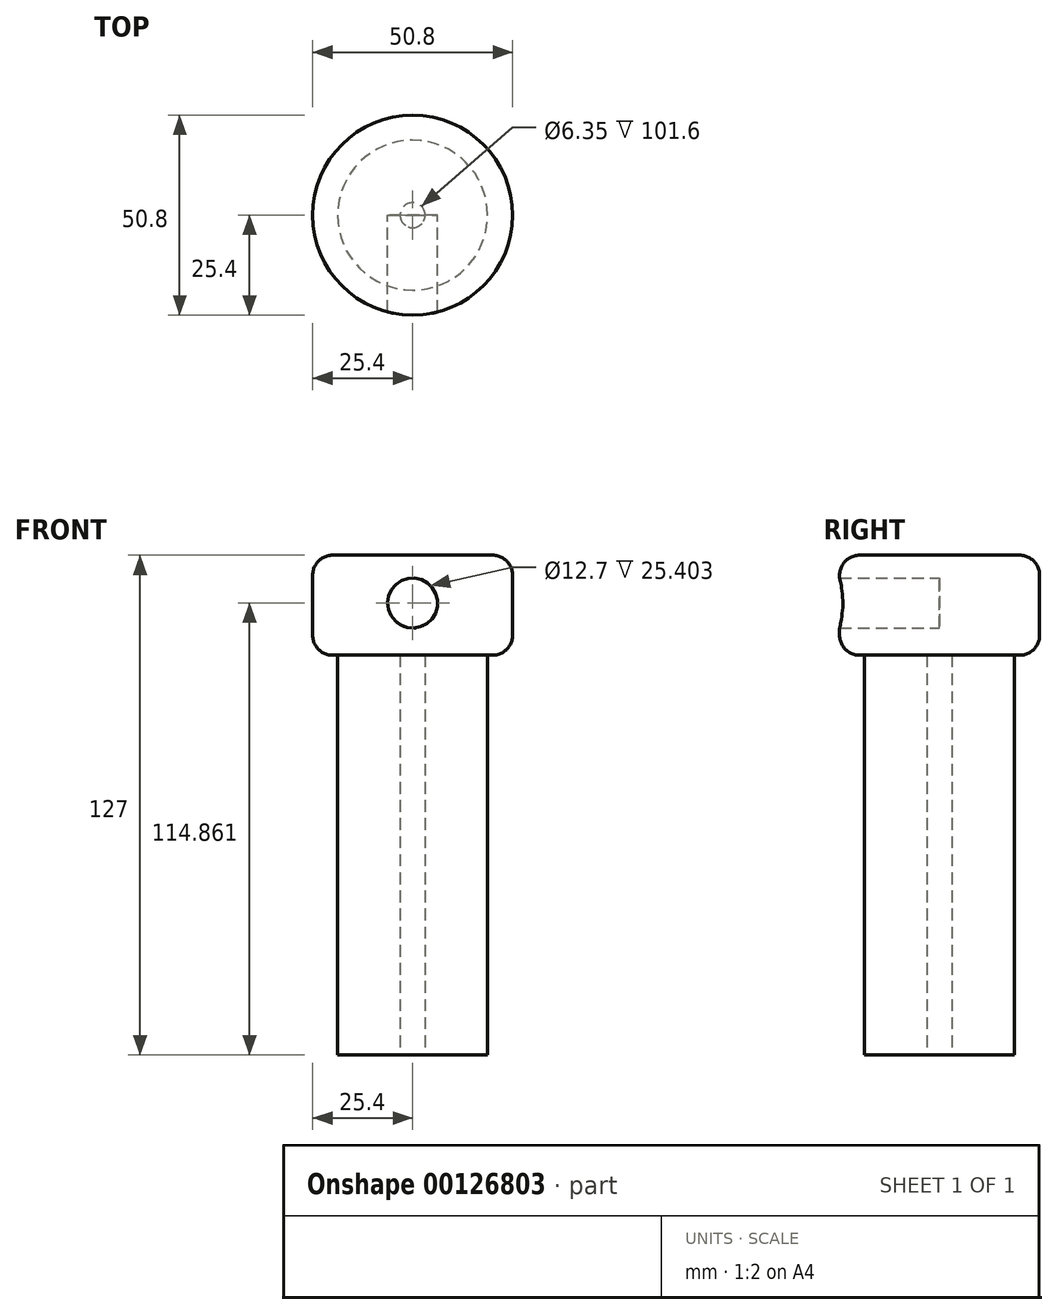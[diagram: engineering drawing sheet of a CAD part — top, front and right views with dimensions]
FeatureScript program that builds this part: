
annotation { "Feature Type Name" : "Feature", "Feature Type Description" : "" }
export const myFeature = defineFeature(function(context is Context, id is Id, definition is map)
    precondition{}
    {
        {
            var Q0;
            Q0=qCreatedBy(makeId("Top.planeOp"),FACE);
            var sketch = newSketch(context, id + "F0", { "sketchPlane" : qUnion([Q0])});
            skCircle(sketch, "E0", {"center": v(0, 0) * mm, "radius": 19.05 * mm});
            skSolve(sketch);
        }
        {
            var Q0;
            Q0 = qSketchRegion(id + "F0", true);
            extrude(context, id + "F1", {"entities" : qUnion([Q0]), "depth" : 101.6 * mm});
        }
        {
            var Q0;
            Q0=makeQuery(id+"F1.opExtrude","CAP_FACE",FACE,{"disambiguationData":[OSD([sQuery(id+"F0.wireOp",EDGE,"E0")])],"isStart":true});
            var sketch = newSketch(context, id + "F2", { "sketchPlane" : qUnion([Q0])});
            skPoint(sketch, "E1", {"position": v(0, 0) * mm});
            skSolve(sketch);
        }
        {
            var Q0;
            Q0=sQuery(id+"F2.wireOp",VERTEX,"E1");
            var Q1;
            Q1=makeQuery(id+"F1.opExtrude","SWEPT_BODY",BODY,{"disambiguationData":[OSD([sQuery(id+"F0.wireOp",EDGE,"E0")])]});
            hole(context, id + "F3", {"style" : HoleStyle.SIMPLE, "endStyle" : HoleEndStyle.THROUGH, "holeDiameter" : 6.35 * mm, "locations" : qUnion([Q0]), "scope" : qUnion([Q1]), "isTappedThrough" : true});
        }
        {
            var Q0;
            Q0=makeQuery(id+"F1.opExtrude","CAP_FACE",FACE,{"disambiguationData":[OSD([sQuery(id+"F0.wireOp",EDGE,"E0")])],"isStart":false});
            var sketch = newSketch(context, id + "F4", { "sketchPlane" : qUnion([Q0])});
            skCircle(sketch, "E2", {"center": v(0, 0) * mm, "radius": 25.4 * mm});
            skSolve(sketch);
        }
        {
            var Q0;
            Q0 = qSketchRegion(id + "F4", true);
            extrude(context, id + "F5", {"entities" : qUnion([Q0]), "operationType" : NewBodyOperationType.ADD, "depth" : 25.4 * mm});
        }
        {
            var Q0;
            Q0=qCreatedBy(makeId("Front.planeOp"),FACE);
            var sketch = newSketch(context, id + "F6", { "sketchPlane" : qUnion([Q0])});
            skCircle(sketch, "E3", {"center": v(0, 114.86) * mm, "radius": 6.35 * mm});
            skSolve(sketch);
        }
        {
            var Q0;
            Q0 = qSketchRegion(id + "F6", true);
            extrude(context, id + "F7", {"entities" : qUnion([Q0]), "operationType" : NewBodyOperationType.REMOVE, "depth" : 25.4 * mm});
        }
        {
            var Q0;
            Q0=makeQuery(id+"F7.boolean.opBoolean","COPY",FACE,{"derivedFrom":makeQuery(id+"F7.opExtrude","CAP_FACE",FACE,{"disambiguationData":[OSD([sQuery(id+"F6.wireOp",EDGE,"E3")])],"isStart":true})});
            var sketch = newSketch(context, id + "F8", { "sketchPlane" : qUnion([Q0])});
            skCircle(sketch, "E4", {"center": v(0, 114.86) * mm, "radius": 6.35 * mm});
            skPoint(sketch, "E4.first.point", {"position": v(-3.5, 120.16) * mm});
            skPoint(sketch, "E4.second.point", {"position": v(6.3, 115.65) * mm});
            skPoint(sketch, "E4.third.point", {"position": v(-1.72, 108.75) * mm});
            skSolve(sketch);
        }
        {
            var Q0;
            Q0 = qSketchRegion(id + "F8", true);
            extrude(context, id + "F9", {"entities" : qUnion([Q0]), "operationType" : NewBodyOperationType.REMOVE, "depth" : 127 * mm});
        }
        {
            var Q0;
            Q0=makeQuery(id+"F5.opExtrude","CAP_EDGE",EDGE,{"disambiguationData":[OSD([sQuery(id+"F4.wireOp",EDGE,"E2")])],"isStart":true});
            var Q1;
            Q1=makeQuery(id+"F5.opExtrude","CAP_EDGE",EDGE,{"disambiguationData":[OSD([sQuery(id+"F4.wireOp",EDGE,"E2")])],"isStart":false});
            fillet(context, id + "F10", {"entities" : qUnion([Q0, Q1]), "radius" : 5.08 * mm, "tangentPropagation" : true, "allowEdgeOverflow" : false});
        }
    });
